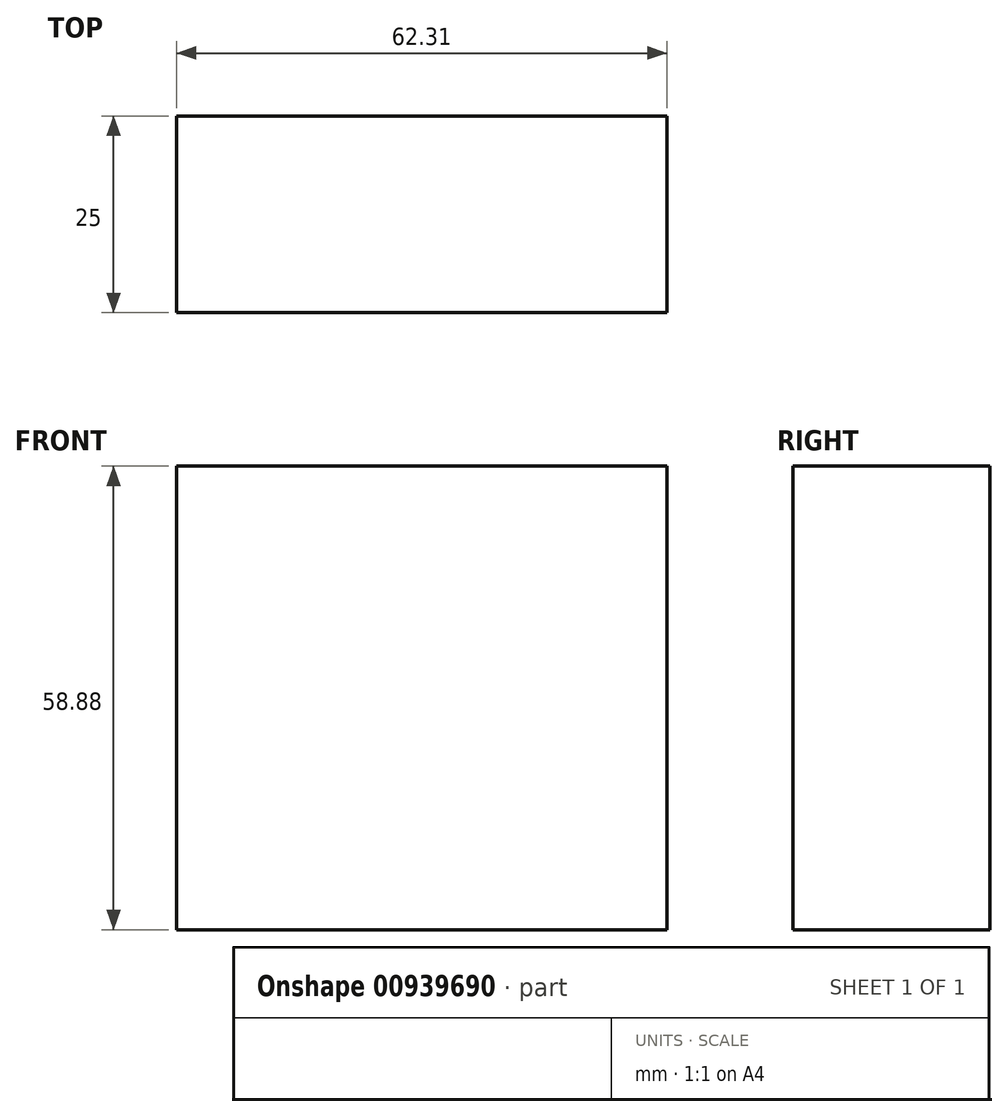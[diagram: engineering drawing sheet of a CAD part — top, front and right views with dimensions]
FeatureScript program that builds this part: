
annotation { "Feature Type Name" : "Feature", "Feature Type Description" : "" }
export const myFeature = defineFeature(function(context is Context, id is Id, definition is map)
    precondition{}
    {
        {
            var Q0;
            Q0=qCreatedBy(makeId("Front.planeOp"),FACE);
            var sketch = newSketch(context, id + "F0", { "sketchPlane" : qUnion([Q0])});
            skLineSegment(sketch, "E0.bottom", {"start": v(-137.77, -6.83) * mm, "end": v(-75.46, -6.83) * mm});
            skLineSegment(sketch, "E0.top", {"start": v(-137.77, 52.05) * mm, "end": v(-75.46, 52.05) * mm});
            skLineSegment(sketch, "E0.left", {"start": v(-137.77, -6.83) * mm, "end": v(-137.77, 52.05) * mm});
            skLineSegment(sketch, "E0.right", {"start": v(-75.46, -6.83) * mm, "end": v(-75.46, 52.05) * mm});
            skPoint(sketch, "E0.middle", {"position": v(-106.62, 22.61) * mm});
            skSolve(sketch);
        }
        {
            var Q0;
            Q0=makeQuery(id+"F0.imprint","IMPRINT",FACE,{"disambiguationData":[TD([[makeQuery(id+"F0.imprint","IMPRINT",EDGE,{"derivedFrom":sQuery(id+"F0.wireOp",EDGE,"E0.bottom")}),1.0]])]});
            extrude(context, id + "F1", {"entities" : qUnion([Q0]), "depth" : 25 * mm, "offsetDistance" : 25 * mm});
        }
    });
